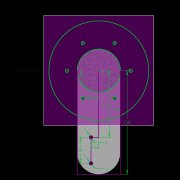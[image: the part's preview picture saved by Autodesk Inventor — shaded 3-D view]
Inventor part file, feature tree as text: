
AUTODESK INVENTOR PART (.ipt)
format: ipt  version: 2022.2 (Build 262287010, 287A)  size: 877,568 bytes
history: native  units: mm
features: extrude x31, other x20, sketch x18, pattern_circular x11, plane x5, fillet x3, draft x3, move_body x2, revolve x2, chamfer x2
ambient origin geometry x8: Origin, YZ Plane, XZ Plane, XY Plane, X Axis, Y Axis, Z Axis, Center Point
bodies: Solid5 (feature_tree)
feature tree (97):
  other  "CrossSection1"
  other  "CrossSection2"
  sketch  "Sketch7"  dims[d167=8.972256mm]
  other  "Roller1"
  other  "Roller2"
  sketch  "Sketch22"  dims[d173=10.814812mm]
  sketch  "Sketch2"  dims[d57=4.025mm d90=61.984365mm]
  sketch  "Sketch23"  dims[d201=75.0mm d232=0.0mm d233=3600.0mm]
  other  "RevRoller1"
  fillet  "Fillet1"  Radius=59.246882mm
  extrude  "Extrusion39"  Depth=61.984365mm
  pattern_circular  "Circular Pattern13"  Count=360  [1 undecoded]
  move_body  "Move Body7"
  revolve  "Revolution13"  [1 undecoded]
  fillet  "Fillet3"  Radius=0.025mm
  pattern_circular  "Circular Pattern14"  Count=24  [1 undecoded]
  move_body  "Move Body6"
  revolve  "Revolution14"  [1 undecoded]
  other  "OuterRim_Top2"
  other  "OuterRim_Bottom2"
  plane  "Work Plane8"
  sketch  "Sketch49"  dims[d352=0.025mm]
  sketch  "Sketch50"  dims[d354=0.025mm]
  sketch  "Sketch51"  dims[d355=16.1595mm]
  extrude  "Extrusion40"  Depth=0.75mm
  extrude  "Extrusion41"  Depth=0.75mm
  extrude  "Extrusion42"  Depth=1.0mm
  extrude  "Extrusion43"  Depth=0.75mm
  sketch  "Sketch52"  dims[d356=16.159664mm]
  extrude  "Extrusion44"  TaperAngle=90.0deg  [1 undecoded]
  extrude  "Extrusion45"  Depth=0.75mm
  extrude  "Extrusion46"  Depth=0.75mm
  extrude  "Extrusion47"  TaperAngle=360.0deg  [1 undecoded]
  pattern_circular  "Circular Pattern32"  Angle=90.0deg  [1 undecoded]
  pattern_circular  "Circular Pattern33"  [2 undecoded]
  sketch  "Sketch57"  dims[d358=360.0deg]
  extrude  "Extrusion50"  Depth=0.75mm
  extrude  "Extrusion51"  Depth=0.75mm
  pattern_circular  "Circular Pattern34"  [2 undecoded]
  extrude  "Extrusion52"  Depth=0.75mm
  extrude  "Extrusion53"  Depth=11.193516mm
  pattern_circular  "Circular Pattern35"  [2 undecoded]
  plane  "Work Plane9"
  sketch  "Sketch59"  dims[d361=360.0deg d363=1.308997mm d367=8.1mm d370=0.025mm d371=1.0mm d372=1.308997mm d373=90.0deg d374=0.5mm d375=240.0mm d376=360.0deg d378=90.0deg d379=0.1mm d380=0.025mm d381=0.025mm d382=0.025mm d383=0.025mm d384=11.193516mm d385=0.0mm d386=0.0mm d391=25.0mm d392=75.0mm d393=1.5mm d394=1.5mm d395=1.5mm d396=1.5mm d397=90.0deg d398=90.0deg d399=90.0deg d400=75.0mm d401=11.193516mm d402=0.0mm d486=0.436332mm d487=0.5mm d488=2.0mm d489=0.0mm d490=20.0mm d495=2.5mm d496=8.0mm d506=13.856406mm d507=55.5mm d508=8.0mm d509=0.05mm d510=2.5mm d511=30.0deg d512=12.0mm d513=6.0mm d514=0.2mm d515=30.0deg d516=131.0mm d517=65.5mm d518=0.2mm d519=100.0mm d520=120.0mm d521=2.0mm d522=150.0mm d530=50.0mm d531=5.5mm d532=5.5mm d533=5.5mm d534=85.75mm d535=73.5mm d536=61.25mm d537=24.5mm d538=3.0mm d539=2.4mm d540=0.0mm d541=0.0mm d542=0.0mm d543=5.5mm d544=3.0mm d545=0.0mm d546=90.0mm d547=360.0deg d549=3.0mm d550=3.0mm d551=2.4mm d552=0.0mm d553=5.596758mm d554=0.0mm d555=2.4mm d556=0.0mm d557=5.596758mm d558=0.0mm d559=5.596758mm d560=0.0mm d561=90.0mm d562=360.0deg d564=60.0mm d565=360.0deg d567=5.5mm d568=5.5mm d569=3.0mm d570=0.0mm d571=5.596758mm d572=0.0mm d573=3.0mm d574=0.0mm d575=5.596758mm d576=0.0mm d577=90.0mm d578=360.0deg d580=60.0mm d581=360.0deg d584=20.0mm d585=8.0mm d587=1.75mm d589=3.0mm d592=2.0mm d593=12.0mm d594=12.0mm d600=0.5mm d601=2.0mm d602=45.0deg d603=0.5mm d604=2.0mm d605=45.0deg d606=0.436332mm d607=0.5mm d608=0.0mm d609=20.0mm d611=360.0deg d613=0.0mm d614=0.0mm d617=0.99971mm d618=100.0mm d620=69.0mm d621=5.0mm d622=0.5mm d623=0.5mm d624=5.0mm d625=0.2mm d626=0.0mm d627=20.0mm d629=69.0mm d630=73.5mm d631=20.0mm d633=6.283185mm d635=5.5mm d636=3.0mm d637=7.0mm d638=4.0mm d639=5.596758mm d640=0.0mm d641=3.0mm d642=0.0mm d643=5.596758mm d644=0.0mm d645=4.0mm d646=0.0mm d647=20.0mm d649=6.283185mm d651=3.0mm d652=4.0mm d653=20.0mm d655=6.283185mm d657=7.0mm d658=5.5mm d659=5.596758mm d660=0.0mm d661=2.593516mm d662=0.0mm d663=5.596758mm d664=0.0mm d665=3.193516mm d666=0.0mm d679=50.0mm d680=360.0deg d682=50.0mm d683=360.0deg d694=6.35mm d695=6.35mm d696=6.9mm d697=5.9mm d698=11.194mm d699=0.0mm d700=8.194mm d701=0.0mm d702=60.0mm d703=360.0deg d705=30.0deg d706=4.0mm d707=7.0mm d708=3.193516mm d709=0.0mm d710=11.193516mm d711=0.0mm d712=60.0mm d713=360.0deg d715=20.0mm d716=77.0mm d717=9.0mm d718=30.0mm d719=4.0mm d720=4.0mm d721=120.0mm d722=90.0deg d723=1.0mm d724=0.0mm d734=0.436332mm d737=1.0mm d738=0.0mm d739=1.0mm d740=0.0mm d741=25.0mm d742=0.5mm d743=2.0mm d744=0.0mm d745=20.0mm d16=0.872665mm d17=0.872665mm d49=0.872665mm d50=0.872665mm d51=0.872665mm d52=0.872665mm d236=0.5mm d237=0.872665mm d238=0.5mm d239=0.872665mm d282=1.0mm d283=1.0mm d284=1.0mm d285=0.15mm d286=0.25mm d287=0.375mm d288=14.3117mm d289=0.75mm d290=20.594885mm d291=0.0625mm d292=0.75mm d293=0.375mm d405=0.5mm d406=0.872665mm d407=0.5mm d408=0.872665mm d413=0.5mm d414=0.872665mm d415=0.5mm d416=0.872665mm d417=0.5mm d418=0.872665mm d419=0.5mm d420=0.872665mm d421=0.872665mm d431=0.5mm d432=0.872665mm d433=0.5mm d434=0.872665mm d471=0.5mm d472=0.872665mm d473=0.5mm d474=0.872665mm d497=0.5mm d498=0.872665mm d499=0.5mm d500=0.872665mm d590=0.5mm d591=0.872665mm d729=0.5mm d730=0.872665mm d731=0.5mm d732=0.872665mm]
  extrude  "Extrusion54"  TaperAngle=0.0deg  [1 undecoded]
  draft  "FaceDraft7"
  extrude  "Extrusion59"  Depth=25.0mm
  extrude  "Extrusion60"  Depth=75.0mm
  fillet  "Fillet5"  Radius=1.5mm
  plane  "Work Plane7"
  sketch  "Sketch47"  dims[d350=47.575427mm]
  extrude  "Rotor_Ring"  Depth=1.5mm
  draft  "FaceDraft2"
  sketch  "Sketch30"  dims[d343=16.1595mm d344=16.159664mm d345=0.025mm]
  plane  "Work Plane5"
  other  "Rotor Featurs"
  other  "RotorRim_Bottom"
  extrude  "Extrusion24"  Depth=1.5mm
  extrude  "Extrusion25"  Depth=1.5mm
  extrude  "Extrusion26"  TaperAngle=90.0deg  [1 undecoded]
  pattern_circular  "Circular Pattern23"  Angle=90.0deg  [1 undecoded]
  sketch  "Sketch41"  dims[d347=0.1mm]
  extrude  "Extrusion27"  TaperAngle=90.0deg  [1 undecoded]
  extrude  "Extrusion28"  Depth=75.0mm
  pattern_circular  "Circular Pattern24"  [2 undecoded]
  extrude  "Extrusion29"  TaperAngle=0.0deg  [1 undecoded]
  extrude  "Extrusion30"  Depth=0.75mm
  extrude  "Extrusion31"  Depth=2.0mm TaperAngle=0.0deg
  pattern_circular  "Circular Pattern25"  [2 undecoded]
  sketch  "Sketch42"  dims[d348=0.1mm]
  extrude  "Extrusion32"  Depth=8.0mm
  extrude  "Extrusion33"  Depth=8.0mm
  extrude  "Extrusion34"  Depth=0.75mm TaperAngle=30.0deg
  extrude  "Extrusion35"  Depth=0.75mm
  pattern_circular  "Circular Pattern26"  Angle=30.0deg  [1 undecoded]
  pattern_circular  "Circular Pattern27"  [2 undecoded]
  chamfer  "Chamfer1"  Distance=65.5mm
  chamfer  "Chamfer2"  Distance=0.2mm
  draft  "FaceDraft4"
  plane  "Work Plane6"
  sketch  "Sketch43"  dims[d349=47.575591mm]
  extrude  "Extrusion37"  Depth=0.75mm
  extrude  "Extrusion38"  Depth=2.0mm
  other  "2D Equation Curve1"
  sketch  "Sketch40"  dims[d346=0.025mm]
  other  "Work Axis6"
  other  "Work Axis7"
  other  "Work Axis8"
  other  "Work Axis9"
  other  "Work Axis10"
  other  "Work Point1"
  other  "Work Point2"
  other  "Work Point3"
  other  "Work Point4"
  other  "Work Point5"
  sketch  "Sketch48"  dims[d351=0.025mm]
  sketch  "Sketch58"  dims[d359=0.5mm d360=240.0mm]
note: 25 required parameter values undecoded (feature->parameter linkage not recoverable at this tier; creation-order binding heuristic only, values carry confidence <= 0.55)